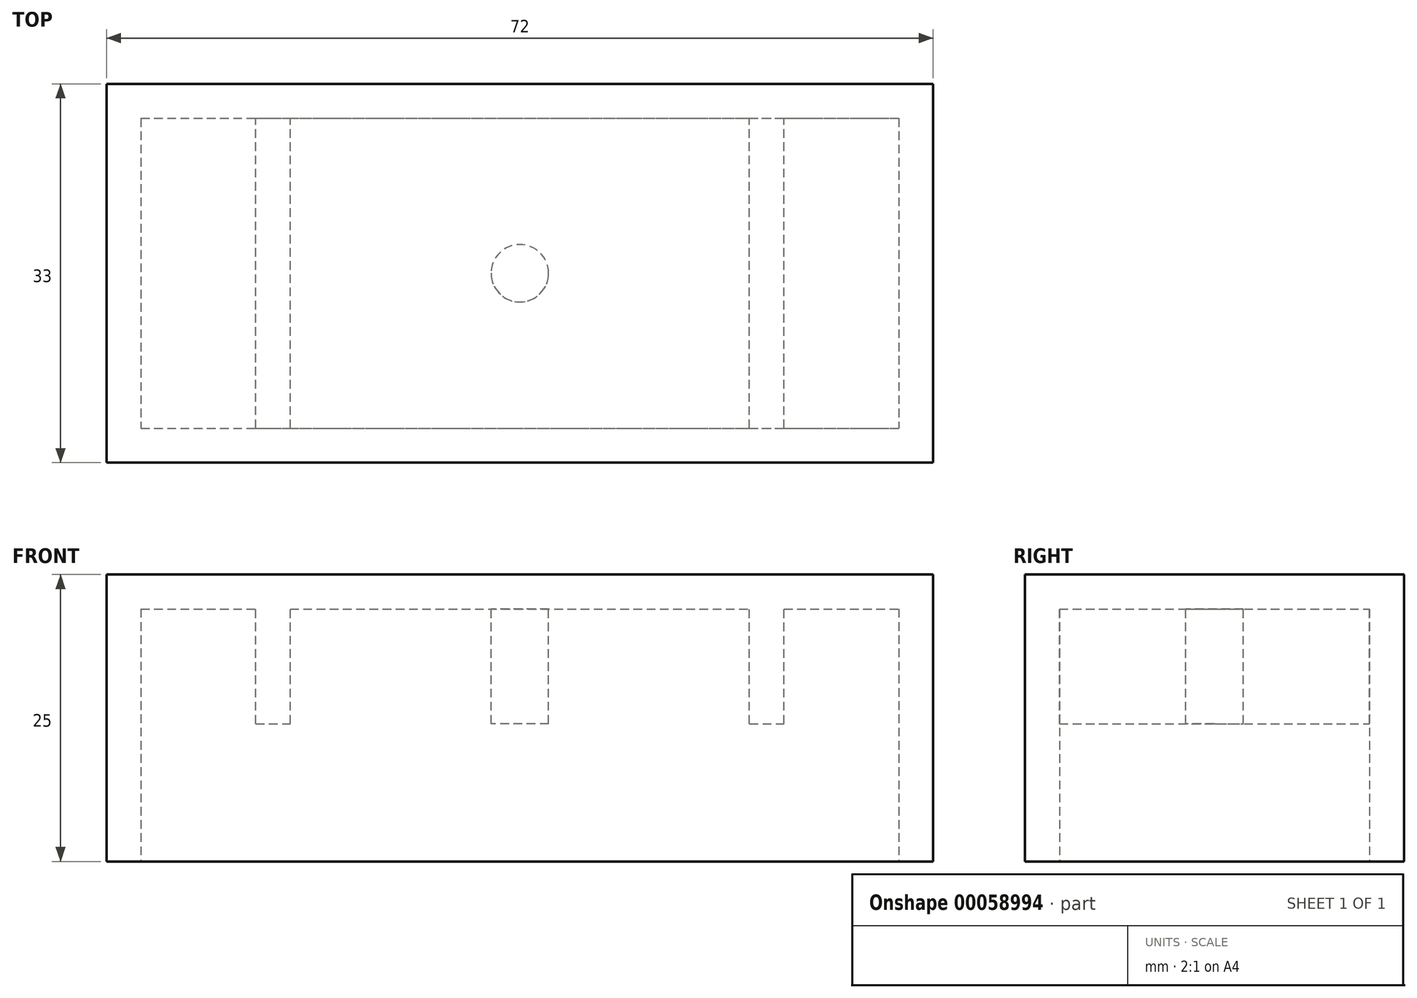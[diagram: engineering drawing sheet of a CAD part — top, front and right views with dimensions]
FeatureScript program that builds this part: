
annotation { "Feature Type Name" : "Feature", "Feature Type Description" : "" }
export const myFeature = defineFeature(function(context is Context, id is Id, definition is map)
    precondition{}
    {
        {
            var Q0;
            Q0=qCreatedBy(makeId("Top.planeOp"),FACE);
            var sketch = newSketch(context, id + "F0", { "sketchPlane" : qUnion([Q0])});
            skLineSegment(sketch, "E0.rect.bottom", {"start": v(-36, 16.5) * mm, "end": v(36, 16.5) * mm});
            skLineSegment(sketch, "E0.rect.top", {"start": v(-36, -16.5) * mm, "end": v(36, -16.5) * mm});
            skLineSegment(sketch, "E0.rect.left", {"start": v(-36, 16.5) * mm, "end": v(-36, -16.5) * mm});
            skLineSegment(sketch, "E0.rect.right", {"start": v(36, 16.5) * mm, "end": v(36, -16.5) * mm});
            skPoint(sketch, "E0.rect.middle", {"position": v(0, 0) * mm});
            skSolve(sketch);
        }
        {
            var Q0;
            Q0=makeQuery(id+"F0.imprint","IMPRINT",FACE,{"disambiguationData":[TD([[makeQuery(id+"F0.imprint","IMPRINT",EDGE,{"derivedFrom":sQuery(id+"F0.wireOp",EDGE,"E0.rect.bottom")}),-1.0]])]});
            extrude(context, id + "F1", {"entities" : qUnion([Q0]), "depth" : 25 * mm});
        }
        {
            var Q0;
            Q0=makeQuery(id+"F1.opExtrude","CAP_FACE",FACE,{"disambiguationData":[OSD([sQuery(id+"F0.wireOp",EDGE,"E0.rect.bottom"),sQuery(id+"F0.wireOp",EDGE,"E0.rect.top"),sQuery(id+"F0.wireOp",EDGE,"E0.rect.left"),sQuery(id+"F0.wireOp",EDGE,"E0.rect.right")])],"isStart":true});
            shell(context, id + "F2", {"entities" : qUnion([Q0]), "thickness" : 3 * mm});
        }
        {
            var Q0;
            Q0=makeQuery(id+"F2.opShell","OFFSET_FACE",FACE,{"disambiguationData":[OSD([sQuery(id+"F0.wireOp",EDGE,"E0.rect.bottom"),sQuery(id+"F0.wireOp",EDGE,"E0.rect.top"),sQuery(id+"F0.wireOp",EDGE,"E0.rect.left"),sQuery(id+"F0.wireOp",EDGE,"E0.rect.right")])]});
            var sketch = newSketch(context, id + "F3", { "sketchPlane" : qUnion([Q0])});
            skCircle(sketch, "E1", {"center": v(0, 0) * mm, "radius": 2.5 * mm});
            skLineSegment(sketch, "E2.bottom", {"start": v(-23, 13.5) * mm, "end": v(-20, 13.5) * mm});
            skLineSegment(sketch, "E2.top", {"start": v(-23, -13.5) * mm, "end": v(-20, -13.5) * mm});
            skLineSegment(sketch, "E2.left", {"start": v(-23, 13.5) * mm, "end": v(-23, -13.5) * mm});
            skLineSegment(sketch, "E2.right", {"start": v(-20, 13.5) * mm, "end": v(-20, -13.5) * mm});
            skLineSegment(sketch, "E3.MirrorCS", {"start": v(20, 13.5) * mm, "end": v(20, -13.5) * mm});
            skLineSegment(sketch, "E4.MirrorCS", {"start": v(23, 13.5) * mm, "end": v(20, 13.5) * mm});
            skLineSegment(sketch, "E5.MirrorCS", {"start": v(23, 13.5) * mm, "end": v(23, -13.5) * mm});
            skLineSegment(sketch, "E6.MirrorCS", {"start": v(23, -13.5) * mm, "end": v(20, -13.5) * mm});
            skSolve(sketch);
        }
        {
            var Q0;
            Q0 = qSketchRegion(id + "F3", true);
            extrude(context, id + "F4", {"entities" : qUnion([Q0]), "operationType" : NewBodyOperationType.ADD, "depth" : 10 * mm});
        }
    });
